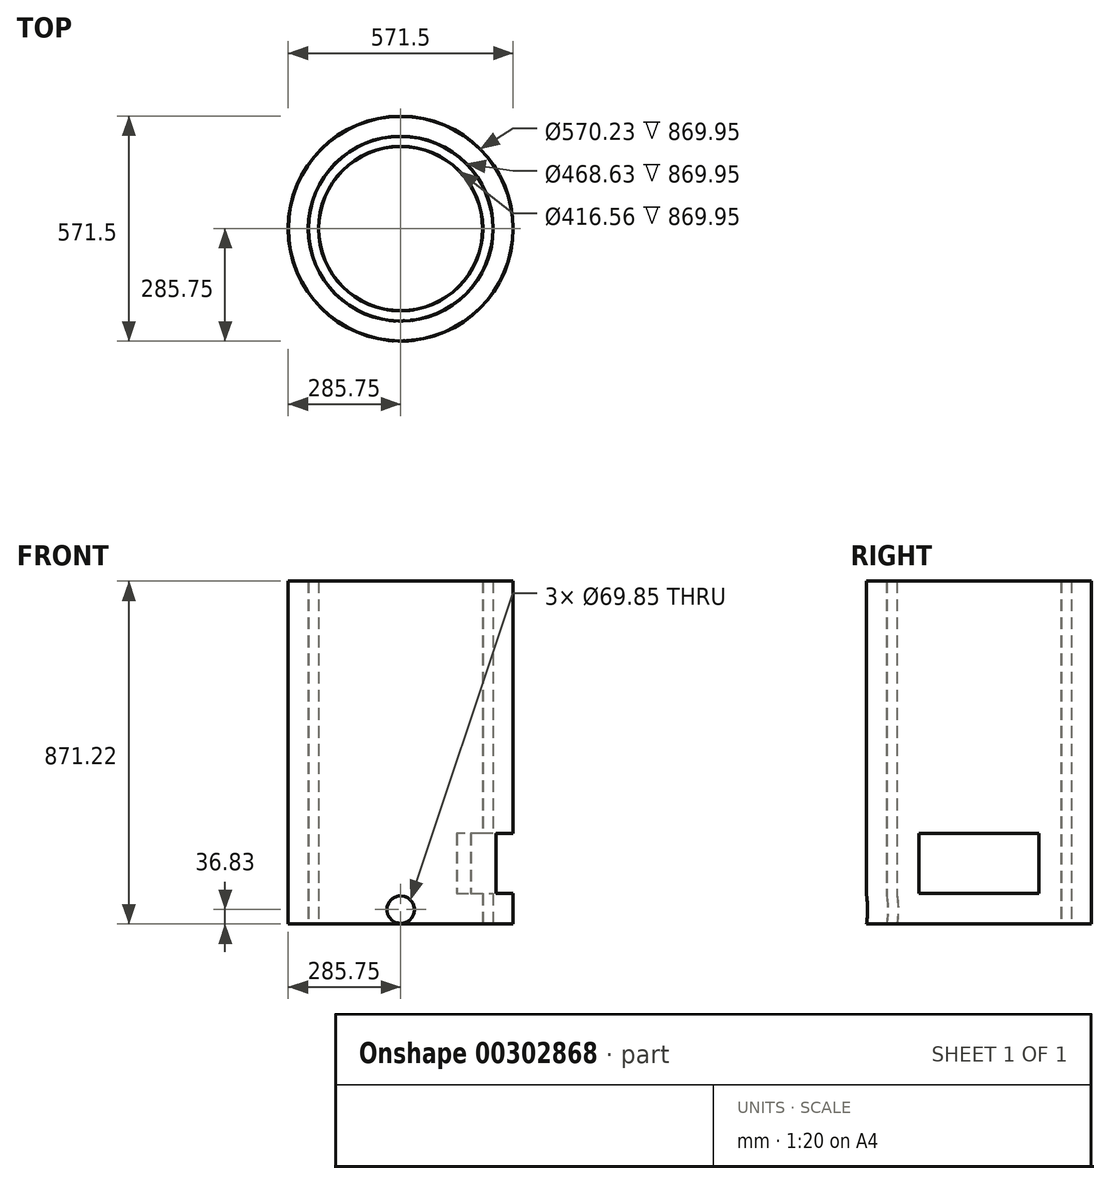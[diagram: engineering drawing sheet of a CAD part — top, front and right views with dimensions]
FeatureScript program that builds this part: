
annotation { "Feature Type Name" : "Feature", "Feature Type Description" : "" }
export const myFeature = defineFeature(function(context is Context, id is Id, definition is map)
    precondition{}
    {
        {
            var Q0;
            Q0=qCreatedBy(makeId("Top.planeOp"),FACE);
            var sketch = newSketch(context, id + "F0", { "sketchPlane" : qUnion([Q0])});
            skCircle(sketch, "E0", {"center": v(0, 0) * mm, "radius": 285.75 * mm});
            skSolve(sketch);
        }
        {
            var Q0;
            Q0 = qSketchRegion(id + "F0", true);
            var Q1;
            Q1=makeQuery(id+"F0.imprint","IMPRINT",FACE,{"disambiguationData":[TD([[makeQuery(id+"F0.imprint","IMPRINT",EDGE,{"derivedFrom":sQuery(id+"F0.wireOp",EDGE,"E0")}),1.0]])]});
            extrude(context, id + "F1", {"entities" : qUnion([Q0, Q1]), "oppositeDirection" : true, "depth" : 1.27 * mm});
        }
        {
            var Q0;
            Q0=makeQuery(id+"F1.opExtrude","CAP_FACE",FACE,{"disambiguationData":[OSD([sQuery(id+"F0.wireOp",EDGE,"E0")])],"isStart":true});
            var sketch = newSketch(context, id + "F2", { "sketchPlane" : qUnion([Q0])});
            skCircle(sketch, "E1", {"center": v(0, 0) * mm, "radius": 285.12 * mm});
            skSolve(sketch);
        }
        {
            var Q0;
            Q0=makeQuery(id+"F2.imprint","IMPRINT",FACE,{"disambiguationData":[TD([[makeQuery(id+"F2.imprint","IMPRINT",EDGE,{"derivedFrom":sQuery(id+"F2.wireOp",EDGE,"E1")}),-1.0]])]});
            extrude(context, id + "F3", {"entities" : qUnion([Q0]), "operationType" : NewBodyOperationType.ADD, "depth" : 869.95 * mm});
        }
        {
            var Q0;
            Q0=makeQuery(id+"F1.opExtrude","CAP_FACE",FACE,{"disambiguationData":[OSD([sQuery(id+"F0.wireOp",EDGE,"E0")])],"isStart":true});
            var sketch = newSketch(context, id + "F4", { "sketchPlane" : qUnion([Q0])});
            skCircle(sketch, "E2", {"center": v(0, 0) * mm, "radius": 234.95 * mm});
            skCircle(sketch, "E3", {"center": v(0, 0) * mm, "radius": 234.32 * mm});
            skSolve(sketch);
        }
        {
            var Q0;
            Q0=makeQuery(id+"F4.imprint","IMPRINT",FACE,{"disambiguationData":[TD([[makeQuery(id+"F4.imprint","IMPRINT",EDGE,{"derivedFrom":sQuery(id+"F4.wireOp",EDGE,"E2")}),1.0]])]});
            extrude(context, id + "F5", {"entities" : qUnion([Q0]), "operationType" : NewBodyOperationType.ADD, "depth" : 869.95 * mm});
        }
        {
            var Q0;
            Q0=makeQuery(id+"F5.boolean.opBoolean","SPLIT",FACE,{"disambiguationData":[TD([makeQuery(id+"F5.opExtrude","SWEPT_FACE",FACE,{"disambiguationData":[OSD([sQuery(id+"F4.wireOp",EDGE,"E3")])]})])],"derivedFrom":makeQuery(id+"F1.opExtrude","CAP_FACE",FACE,{"disambiguationData":[OSD([sQuery(id+"F0.wireOp",EDGE,"E0")])],"isStart":true})});
            var sketch = newSketch(context, id + "F6", { "sketchPlane" : qUnion([Q0])});
            skCircle(sketch, "E4", {"center": v(0, 0) * mm, "radius": 208.92 * mm});
            skCircle(sketch, "E5", {"center": v(0, 0) * mm, "radius": 208.28 * mm});
            skSolve(sketch);
        }
        {
            var Q0;
            Q0=makeQuery(id+"F6.imprint","IMPRINT",FACE,{"disambiguationData":[TD([[makeQuery(id+"F6.imprint","IMPRINT",EDGE,{"derivedFrom":sQuery(id+"F6.wireOp",EDGE,"E4")}),1.0]])]});
            extrude(context, id + "F7", {"entities" : qUnion([Q0]), "operationType" : NewBodyOperationType.ADD, "depth" : 869.95 * mm});
        }
        {
            var Q0;
            Q0=qCreatedBy(makeId("Front.planeOp"),FACE);
            var sketch = newSketch(context, id + "F8", { "sketchPlane" : qUnion([Q0])});
            skLineSegment(sketch, "E6", {"start": v(0, 0) * mm, "end": v(0, 35.56) * mm});
            skLineSegment(sketch, "E7", {"start": v(0, 35.56) * mm, "end": v(0, 35.56) * mm});
            skCircle(sketch, "E8", {"center": v(0, 35.56) * mm, "radius": 34.93 * mm});
            skSolve(sketch);
        }
        {
            var Q0;
            Q0=makeQuery(id+"F8.imprint","IMPRINT",FACE,{"disambiguationData":[TD([[makeQuery(id+"F8.imprint","IMPRINT",EDGE,{"derivedFrom":sQuery(id+"F8.wireOp",EDGE,"E8")}),1.0]])]});
            extrude(context, id + "F9", {"entities" : qUnion([Q0]), "operationType" : NewBodyOperationType.REMOVE, "endBound" : BoundingType.THROUGH_ALL, "depth" : 304.8 * mm});
        }
        {
            var Q0;
            Q0=qCreatedBy(makeId("Right.planeOp"),FACE);
            var sketch = newSketch(context, id + "F10", { "sketchPlane" : qUnion([Q0])});
            skLineSegment(sketch, "E9", {"start": v(0, 0) * mm, "end": v(0, 76.2) * mm});
            skLineSegment(sketch, "E10", {"start": v(0, 76.2) * mm, "end": v(152.4, 76.2) * mm});
            skLineSegment(sketch, "E11", {"start": v(152.4, 76.2) * mm, "end": v(152.4, 228.6) * mm});
            skLineSegment(sketch, "E12", {"start": v(152.4, 228.6) * mm, "end": v(-152.4, 228.6) * mm});
            skLineSegment(sketch, "E13", {"start": v(-152.4, 228.6) * mm, "end": v(-152.4, 76.2) * mm});
            skLineSegment(sketch, "E14", {"start": v(-152.4, 76.2) * mm, "end": v(0, 76.2) * mm});
            skSolve(sketch);
        }
        {
            var Q0;
            Q0=makeQuery(id+"F10.imprint","IMPRINT",FACE,{"disambiguationData":[TD([[makeQuery(id+"F10.imprint","IMPRINT",EDGE,{"derivedFrom":sQuery(id+"F10.wireOp",EDGE,"E10")}),1.0]])]});
            extrude(context, id + "F11", {"entities" : qUnion([Q0]), "operationType" : NewBodyOperationType.REMOVE, "depth" : 304.8 * mm});
        }
    });
